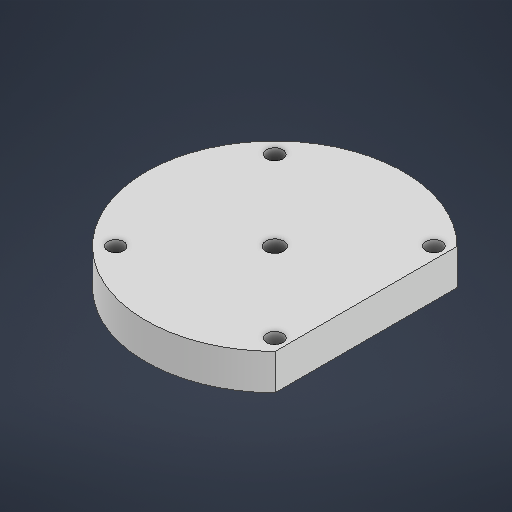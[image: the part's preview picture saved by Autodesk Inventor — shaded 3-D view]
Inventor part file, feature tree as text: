
AUTODESK INVENTOR PART (.ipt)
format: ipt  version: 2025 (Build 290162000, 162)  size: 203,264 bytes
history: native  units: in
note: dims shown in document units (in); Inventor stores cm internally (conversion verified against a paired STEP export)
features: extrude x2, sketch x2
ambient origin geometry x8: Origin, YZ Plane, XZ Plane, XY Plane, X Axis, Y Axis, Z Axis, Center Point
bodies: Solid1 (feature_tree)
feature tree (4):
  extrude  "Extrusion1"  Depth=1.75in
  extrude  "Extrusion2"  Depth=0.3937in
  sketch  "Sketch1"  dims[d0=2.8346in d1=1.75in]
  sketch  "Sketch2"  dims[d2=1.75in d3=2.5591in d4=0.1772in d5=0.1772in d6=0.1772in d7=0.1772in d9=1.0044in d10=0.1294in d11=0.3937in d12=0.0in d13=0.1969in d14=0.3937in d15=0.0in]
